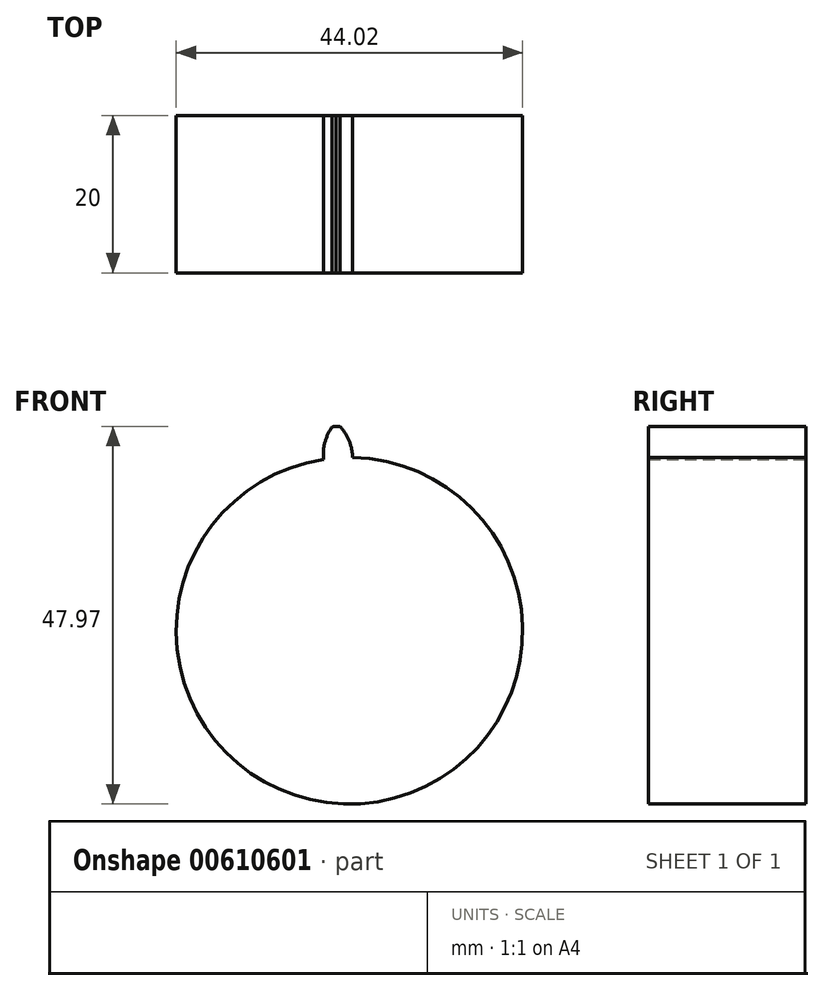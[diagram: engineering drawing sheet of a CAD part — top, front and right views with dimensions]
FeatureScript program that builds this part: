
annotation { "Feature Type Name" : "Feature", "Feature Type Description" : "" }
export const myFeature = defineFeature(function(context is Context, id is Id, definition is map)
    precondition{}
    {
        {
            var Q0;
            Q0=qCreatedBy(makeId("Front.planeOp"),FACE);
            var sketch = newSketch(context, id + "F0", { "sketchPlane" : qUnion([Q0])});
            skCircle(sketch, "E0", {"center": v(0, 0) * mm, "radius": 22 * mm});
            skArc(sketch, "E1", {"start": v(0, 24.04) * mm, "mid": v(-0.52, 25.05) * mm, "end": v(-1.2, 25.96) * mm});
            skArc(sketch, "E2", {"start": v(0.4, 22) * mm, "mid": v(0.3, 23.04) * mm, "end": v(0, 24.04) * mm});
            skArc(sketch, "E3.MirrorCS", {"start": v(-3.14, 23.83) * mm, "mid": v(-2.75, 24.92) * mm, "end": v(-2.17, 25.92) * mm});
            skArc(sketch, "E4.MirrorCS", {"start": v(-3.27, 21.76) * mm, "mid": v(-3.3, 22.8) * mm, "end": v(-3.14, 23.83) * mm});
            skArc(sketch, "E5", {"start": v(-1.2, 25.96) * mm, "mid": v(-1.7, 25.94) * mm, "end": v(-2.17, 25.92) * mm});
            skCircle(sketch, "E6", {"center": v(0, 0) * mm, "radius": 26 * mm});
            skSolve(sketch);
        }
        {
            var Q0;
            {var subQ0=sQuery(id+"F0.wireOp",EDGE,"E0");var subQ1=makeQuery(id+"F0.imprint","INTERSECT",VERTEX,{"derivedFrom":[subQ0,sQuery(id+"F0.wireOp",EDGE,"E2")]});Q0=makeQuery(id+"F0.imprint","IMPRINT",FACE,{"disambiguationData":[TD([[makeQuery(id+"F0.imprint","IMPRINT",EDGE,{"disambiguationData":[TD([[subQ1,-1.0]])],"derivedFrom":subQ0}),1.0]])]});}
            var Q1;
            Q1=makeQuery(id+"F0.imprint","IMPRINT",FACE,{"disambiguationData":[TD([[makeQuery(id+"F0.imprint","IMPRINT",EDGE,{"derivedFrom":sQuery(id+"F0.wireOp",EDGE,"E1")}),1.0]])]});
            extrude(context, id + "F1", {"entities" : qUnion([Q0, Q1]), "depth" : 20 * mm, "offsetDistance" : 25.4 * mm});
        }
    });
